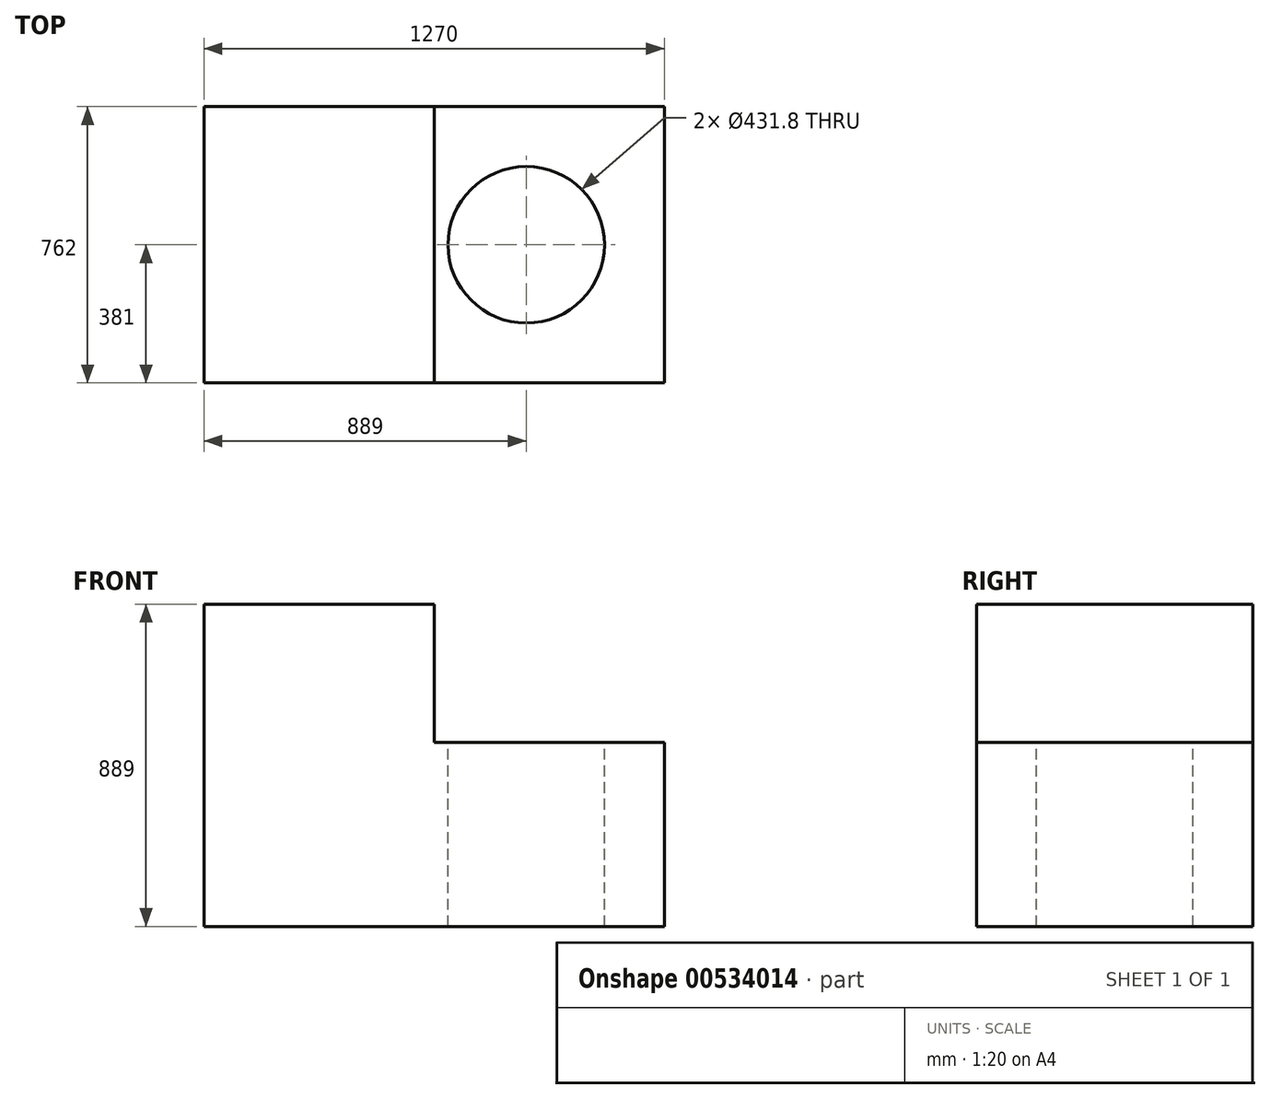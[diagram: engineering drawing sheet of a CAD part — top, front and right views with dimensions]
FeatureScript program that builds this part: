
annotation { "Feature Type Name" : "Feature", "Feature Type Description" : "" }
export const myFeature = defineFeature(function(context is Context, id is Id, definition is map)
    precondition{}
    {
        {
            var Q0;
            Q0=qCreatedBy(makeId("Front.planeOp"),FACE);
            var sketch = newSketch(context, id + "F0", { "sketchPlane" : qUnion([Q0])});
            skLineSegment(sketch, "E0", {"start": v(-635, 0) * mm, "end": v(635, 0) * mm});
            skLineSegment(sketch, "E1", {"start": v(-635, 0) * mm, "end": v(-635, 889) * mm});
            skLineSegment(sketch, "E2", {"start": v(-635, 889) * mm, "end": v(0, 889) * mm});
            skLineSegment(sketch, "E3", {"start": v(0, 889) * mm, "end": v(0, 508) * mm});
            skLineSegment(sketch, "E4", {"start": v(0, 508) * mm, "end": v(635, 508) * mm});
            skLineSegment(sketch, "E5", {"start": v(635, 508) * mm, "end": v(635, 0) * mm});
            skSolve(sketch);
        }
        {
            var Q0;
            Q0 = qSketchRegion(id + "F0", true);
            extrude(context, id + "F1", {"entities" : qUnion([Q0]), "depth" : 762 * mm, "offsetDistance" : 25.4 * mm});
        }
        {
            var Q0;
            Q0=makeQuery(id+"F1.opExtrude","SWEPT_FACE",FACE,{"disambiguationData":[OSD([sQuery(id+"F0.wireOp",EDGE,"E4")])]});
            var sketch = newSketch(context, id + "F2", { "sketchPlane" : qUnion([Q0])});
            skCircle(sketch, "E6", {"center": v(254, -381) * mm, "radius": 215.9 * mm});
            skSolve(sketch);
        }
        {
            var Q0;
            Q0=makeQuery(id+"F2.imprint","IMPRINT",FACE,{"disambiguationData":[TD([[makeQuery(id+"F2.imprint","IMPRINT",EDGE,{"derivedFrom":sQuery(id+"F2.wireOp",EDGE,"E6")}),1.0]])]});
            var Q1;
            Q1=sQuery(id+"F2.wireOp",EDGE,"E6");
            extrude(context, id + "F3", {"entities" : qUnion([Q0]), "operationType" : NewBodyOperationType.REMOVE, "surfaceEntities" : qUnion([Q1]), "endBound" : BoundingType.UP_TO_NEXT, "oppositeDirection" : true, "depth" : 25.4 * mm, "offsetDistance" : 25.4 * mm});
        }
    });
